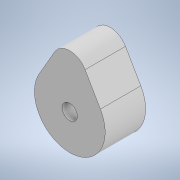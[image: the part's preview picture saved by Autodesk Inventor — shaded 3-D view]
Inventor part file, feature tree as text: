
AUTODESK INVENTOR PART (.ipt)
format: ipt  version: 2021 (Build 250183000, 183)  size: 103,936 bytes
history: native  units: mm
features: extrude x1, sketch x1
ambient origin geometry x8: Origin, YZ Plane, XZ Plane, XY Plane, X Axis, Y Axis, Z Axis, Center Point
bodies: Body1 (feature_tree)
feature tree (2):
  extrude  "Extrusion3"  Depth=7.0mm
  sketch  "Sketch5"  dims[d21=14.0mm d22=7.0mm d23=7.0mm d24=3.0mm d25=8.0mm d26=0.0mm]
